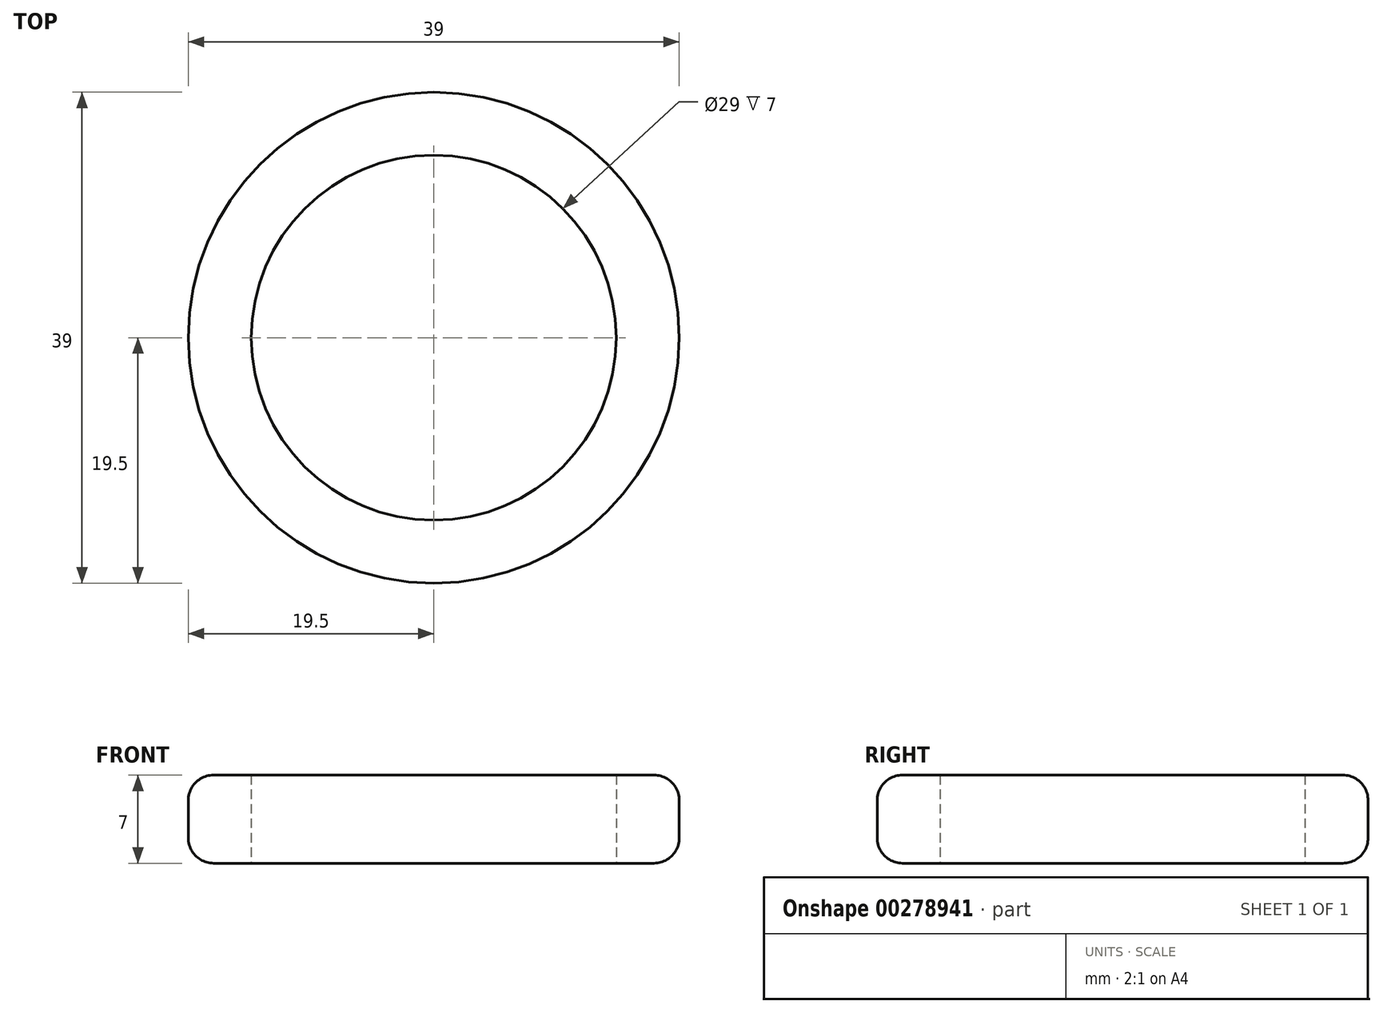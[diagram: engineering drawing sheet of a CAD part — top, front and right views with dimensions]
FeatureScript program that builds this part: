
annotation { "Feature Type Name" : "Feature", "Feature Type Description" : "" }
export const myFeature = defineFeature(function(context is Context, id is Id, definition is map)
    precondition{}
    {
        {
            var Q0;
            Q0=qCreatedBy(makeId("Top.planeOp"),FACE);
            var sketch = newSketch(context, id + "F0", { "sketchPlane" : qUnion([Q0])});
            skCircle(sketch, "E0", {"center": v(0, 0) * mm, "radius": 19.5 * mm});
            skCircle(sketch, "E1", {"center": v(0, 0) * mm, "radius": 14.5 * mm});
            skSolve(sketch);
        }
        {
            var Q0;
            Q0 = qSketchRegion(id + "F0", true);
            extrude(context, id + "F1", {"entities" : qUnion([Q0]), "depth" : 3.5 * mm});
        }
        {
            var Q0;
            Q0=makeQuery(id+"F1.opExtrude","CAP_EDGE",EDGE,{"disambiguationData":[OSD([sQuery(id+"F0.wireOp",EDGE,"E0")])],"isStart":false});
            fillet(context, id + "F2", {"entities" : qUnion([Q0]), "radius" : 2 * mm, "tangentPropagation" : true, "allowEdgeOverflow" : false});
        }
        {
            var Q0;
            Q0=makeQuery(id+"F1.opExtrude","SWEPT_BODY",BODY,{"disambiguationData":[OSD([sQuery(id+"F0.wireOp",EDGE,"E0"),sQuery(id+"F0.wireOp",EDGE,"E1")])]});
            var Q1;
            Q1=qCreatedBy(makeId("Top.planeOp"),FACE);
            mirror(context, id + "F3", {"operationType" : NewBodyOperationType.ADD, "entities" : qUnion([Q0]), "mirrorPlane" : qUnion([Q1])});
        }
    });
